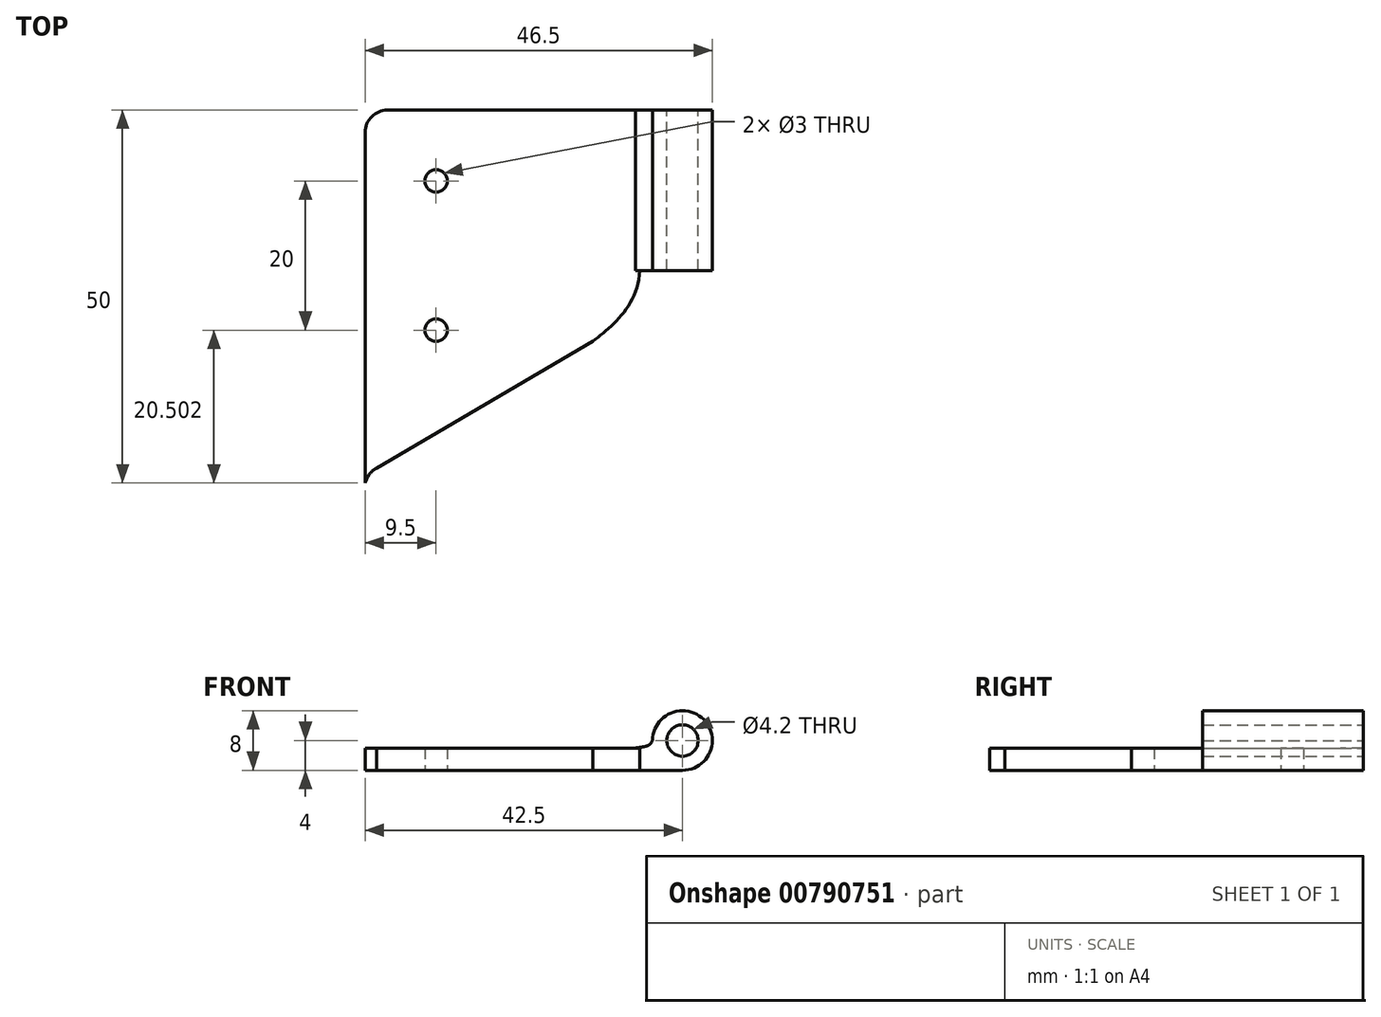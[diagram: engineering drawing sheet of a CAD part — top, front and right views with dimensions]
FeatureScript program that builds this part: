
annotation { "Feature Type Name" : "Feature", "Feature Type Description" : "" }
export const myFeature = defineFeature(function(context is Context, id is Id, definition is map)
    precondition{}
    {
        {
            var Q0;
            Q0=qCreatedBy(makeId("Top.planeOp"),FACE);
            var sketch = newSketch(context, id + "F0", { "sketchPlane" : qUnion([Q0])});
            skLineSegment(sketch, "E0", {"start": v(0, 0) * mm, "end": v(0, 36.16) * mm, "construction": true});
            skLineSegment(sketch, "E1", {"start": v(0, 18.08) * mm, "end": v(-19.25, 18.08) * mm, "construction": true});
            skLineSegment(sketch, "E2", {"start": v(-19.25, 22.25) * mm, "end": v(-19.25, 18.08) * mm, "construction": true});
            skLineSegment(sketch, "E3", {"start": v(0, 35.4) * mm, "end": v(0, 36.16) * mm, "construction": true});
            skLineSegment(sketch, "E4", {"start": v(-17.74, 25) * mm, "end": v(-17.74, 25.76) * mm, "construction": true});
            skLineSegment(sketch, "E5", {"start": v(11.25, 42) * mm, "end": v(11.25, 42.75) * mm, "construction": true});
            skLineSegment(sketch, "E6", {"start": v(-17.74, 25.76) * mm, "end": v(11.25, 42.75) * mm});
            skFitSpline(sketch, "E7", {"points": [v(11.25, 42.75) * mm, v(17.5, 52.25) * mm], "startDerivative": vector(7.33, 5.96) * mm, "endDerivative": vector(0.35, 14.4) * mm});
            skLineSegment(sketch, "E8", {"start": v(11.25, 42) * mm, "end": v(0, 35.4) * mm, "construction": true});
            skLineSegment(sketch, "E9", {"start": v(-17.74, 25) * mm, "end": v(0, 35.4) * mm, "construction": true});
            skLineSegment(sketch, "E10", {"start": v(-19.25, 22.25) * mm, "end": v(-19.25, 23.75) * mm, "construction": true});
            skFitSpline(sketch, "E11", {"points": [v(-17.74, 25.76) * mm, v(-19.25, 23.75) * mm], "startDerivative": vector(-2.6, -1.32) * mm, "endDerivative": vector(-0.72, -2.07) * mm});
            skLineSegment(sketch, "E12", {"start": v(-19.25, 23.75) * mm, "end": v(-19.25, 73.75) * mm});
            skLineSegment(sketch, "E13", {"start": v(-19.25, 73.75) * mm, "end": v(19.25, 73.75) * mm});
            skLineSegment(sketch, "E14", {"start": v(19.25, 73.75) * mm, "end": v(19.25, 52.25) * mm});
            skLineSegment(sketch, "E15", {"start": v(19.25, 52.25) * mm, "end": v(17.5, 52.25) * mm});
            skLineSegment(sketch, "E16", {"start": v(19.25, 52.25) * mm, "end": v(19.25, 51.5) * mm});
            skLineSegment(sketch, "E17", {"start": v(11.25, 42) * mm, "end": v(19.25, 51.5) * mm, "construction": true});
            skSolve(sketch);
        }
        {
            var Q0;
            Q0 = qSketchRegion(id + "F0", true);
            extrude(context, id + "F1", {"entities" : qUnion([Q0]), "depth" : 3 * mm, "offsetDistance" : 25 * mm});
        }
        {
            var Q0;
            Q0=makeQuery(id+"F1.opExtrude","SWEPT_FACE",FACE,{"disambiguationData":[OSD([sQuery(id+"F0.wireOp",EDGE,"E13")])]});
            var sketch = newSketch(context, id + "F2", { "sketchPlane" : qUnion([Q0])});
            skLineSegment(sketch, "E18", {"start": v(-19.25, 0) * mm, "end": v(-23.25, 0) * mm});
            skLineSegment(sketch, "E19", {"start": v(-23.25, 0) * mm, "end": v(-23.25, 4) * mm, "construction": true});
            skCircle(sketch, "E20", {"center": v(-23.25, 4) * mm, "radius": 2.1 * mm});
            skCircle(sketch, "E21", {"center": v(-23.25, 4) * mm, "radius": 4 * mm});
            skLineSegment(sketch, "E22", {"start": v(-19.25, 3) * mm, "end": v(-19.25, 0) * mm});
            skFitSpline(sketch, "E23", {"points": [v(-19.25, 4) * mm, v(-16.97, 3) * mm], "startDerivative": vector(1.1, -2.46) * mm, "endDerivative": vector(3.51, -0.45) * mm});
            skSolve(sketch);
        }
        {
            var Q0;
            Q0 = qSketchRegion(id + "F2", true);
            var Q1;
            {var subQ2=sQuery(id+"F2.wireOp",EDGE,"E18");Q1=makeQuery(id+"F2.imprint","IMPRINT",FACE,{"disambiguationData":[TD([[makeQuery(id+"F2.imprint","IMPRINT",EDGE,{"derivedFrom":subQ2}),-1.0]])]});}
            extrude(context, id + "F3", {"entities" : qUnion([Q0, Q1]), "operationType" : NewBodyOperationType.ADD, "oppositeDirection" : true, "depth" : 21.5 * mm, "offsetDistance" : 25 * mm});
        }
        {
            var Q0;
            Q0=makeQuery(id+"F1.opExtrude","SWEPT_EDGE",EDGE,{"disambiguationData":[OSD([sQuery(id+"F0.wireOp",EDGE,"E12"),sQuery(id+"F0.wireOp",EDGE,"E13")])]});
            fillet(context, id + "F4", {"entities" : qUnion([Q0]), "radius" : 3 * mm, "tangentPropagation" : true, "allowEdgeOverflow" : false});
        }
        {
            var Q0;
            Q0=makeQuery(id+"F3.boolean.opBoolean","MERGE",FACE,{"derivedFrom":[makeQuery(id+"F1.opExtrude","CAP_FACE",FACE,{"disambiguationData":[OSD([sQuery(id+"F0.wireOp",EDGE,"E6"),sQuery(id+"F0.wireOp",EDGE,"E7"),sQuery(id+"F0.wireOp",EDGE,"E11"),sQuery(id+"F0.wireOp",EDGE,"E12"),sQuery(id+"F0.wireOp",EDGE,"E13"),sQuery(id+"F0.wireOp",EDGE,"E14"),sQuery(id+"F0.wireOp",EDGE,"E15")])],"isStart":true}),makeQuery(id+"F3.opExtrude","SWEPT_FACE",FACE,{"disambiguationData":[OSD([sQuery(id+"F2.wireOp",EDGE,"E18")])]})]});
            var sketch = newSketch(context, id + "F5", { "sketchPlane" : qUnion([Q0])});
            skLineSegment(sketch, "E24", {"start": v(-10.2, -73.75) * mm, "end": v(-10.2, -64.25) * mm, "construction": true});
            skLineSegment(sketch, "E25", {"start": v(-19.25, -64.53) * mm, "end": v(-9.75, -64.53) * mm, "construction": true});
            skLineSegment(sketch, "E26", {"start": v(-10.2, -64.25) * mm, "end": v(-9.75, -64.25) * mm, "construction": true});
            skCircle(sketch, "E27", {"center": v(-9.75, -64.25) * mm, "radius": 1.5 * mm});
            skLineSegment(sketch, "E28", {"start": v(-9.75, -64.25) * mm, "end": v(-9.75, -44.25) * mm, "construction": true});
            skCircle(sketch, "E29", {"center": v(-9.75, -44.25) * mm, "radius": 1.5 * mm});
            skSolve(sketch);
        }
        {
            var Q0;
            Q0 = qSketchRegion(id + "F5", true);
            extrude(context, id + "F6", {"entities" : qUnion([Q0]), "operationType" : NewBodyOperationType.REMOVE, "oppositeDirection" : true, "depth" : 3 * mm, "offsetDistance" : 25 * mm});
        }
    });
